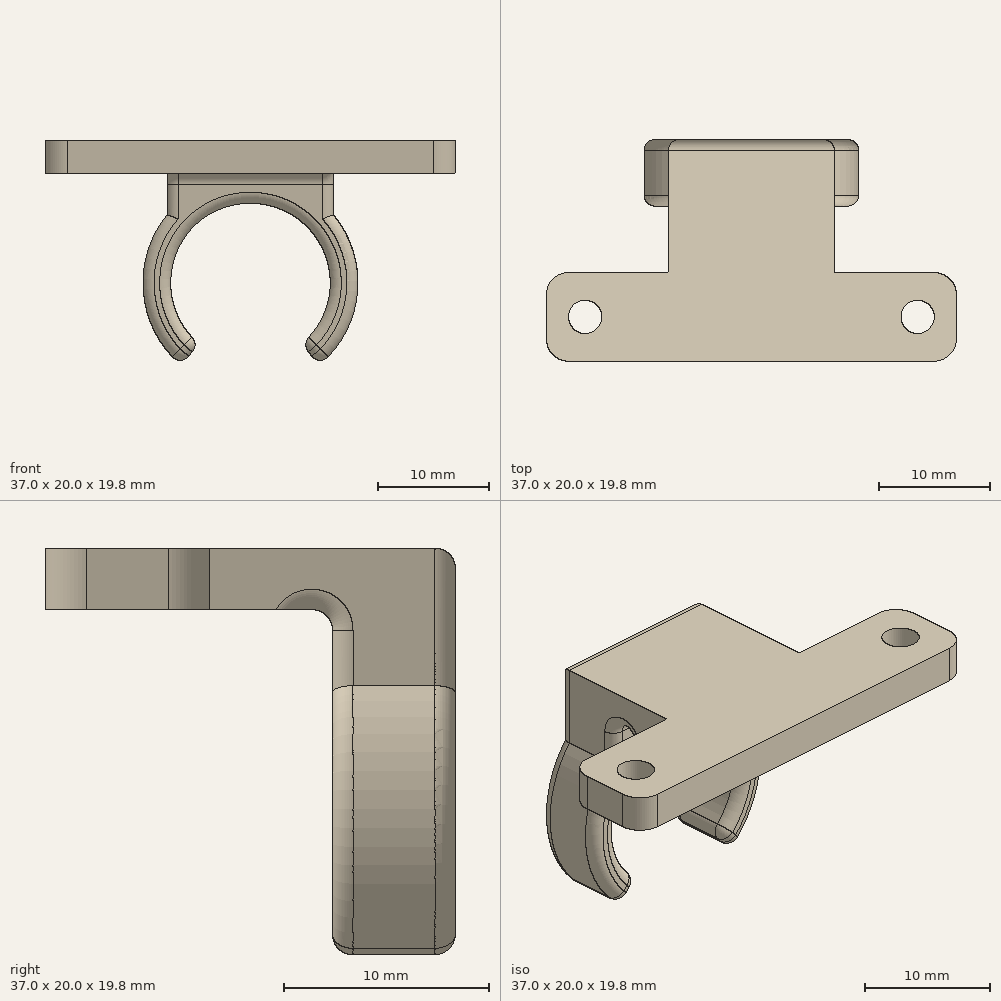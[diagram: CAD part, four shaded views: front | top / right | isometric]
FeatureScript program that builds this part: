
annotation { "Feature Type Name" : "Feature", "Feature Type Description" : "" }
export const myFeature = defineFeature(function(context is Context, id is Id, definition is map)
    precondition{}
    {
        {
            var Q0;
            Q0=qCreatedBy(makeId("Front.planeOp"),FACE);
            var sketch = newSketch(context, id + "F0", { "sketchPlane" : qUnion([Q0])});
            skArc(sketch, "E0", {"start": v(5.27, -4.9) * mm, "mid": v(0, 7.2) * mm, "end": v(-5.27, -4.9) * mm});
            skArc(sketch, "E1.0", {"start": v(7.05, -6.66) * mm, "mid": v(9.7, -0.34) * mm, "end": v(7.5, 6.15) * mm});
            skLineSegment(sketch, "E2", {"start": v(0, 0) * mm, "end": v(6.24, -7.43) * mm, "construction": true});
            skLineSegment(sketch, "E3", {"start": v(5.23, -6.23) * mm, "end": v(5.56, -6.62) * mm});
            skLineSegment(sketch, "E4.MirrorCS", {"start": v(-5.23, -6.23) * mm, "end": v(-5.56, -6.62) * mm});
            skPoint(sketch, "E5.visualSharp", {"position": v(-4.63, -5.52) * mm});
            skArc(sketch, "E5.filletArc", {"start": v(-5.23, -6.23) * mm, "mid": v(-5, -5.57) * mm, "end": v(-5.27, -4.9) * mm});
            skPoint(sketch, "E6.visualSharp", {"position": v(-6.24, -7.43) * mm});
            skArc(sketch, "E6.filletArc", {"start": v(-7.05, -6.66) * mm, "mid": v(-6.3, -6.98) * mm, "end": v(-5.56, -6.62) * mm});
            skPoint(sketch, "E7.visualSharp", {"position": v(4.63, -5.52) * mm});
            skArc(sketch, "E7.filletArc", {"start": v(5.27, -4.9) * mm, "mid": v(5, -5.57) * mm, "end": v(5.23, -6.23) * mm});
            skPoint(sketch, "E8.visualSharp", {"position": v(6.24, -7.43) * mm});
            skArc(sketch, "E8.filletArc", {"start": v(5.56, -6.62) * mm, "mid": v(6.3, -6.98) * mm, "end": v(7.05, -6.66) * mm});
            skLineSegment(sketch, "E9", {"start": v(7.5, 9.86) * mm, "end": v(7.5, 6.15) * mm});
            skArc(sketch, "E10.trimOffspring", {"start": v(-7.5, 6.15) * mm, "mid": v(-9.7, -0.34) * mm, "end": v(-7.05, -6.66) * mm});
            skLineSegment(sketch, "E11", {"start": v(7.5, 9.86) * mm, "end": v(-7.5, 9.86) * mm});
            skLineSegment(sketch, "E12.MirrorCS", {"start": v(-7.5, 9.86) * mm, "end": v(-7.5, 6.15) * mm});
            skSolve(sketch);
        }
        {
            var Q0;
            Q0 = qSketchRegion(id + "F0", true);
            extrude(context, id + "F1", {"entities" : qUnion([Q0]), "depth" : 6 * mm});
        }
        {
            var Q0;
            Q0=makeQuery(id+"F1.opExtrude","CAP_FACE",FACE,{"disambiguationData":[OSD([sQuery(id+"F0.wireOp",EDGE,"E0"),sQuery(id+"F0.wireOp",EDGE,"E1.0"),sQuery(id+"F0.wireOp",EDGE,"E3"),sQuery(id+"F0.wireOp",EDGE,"E4.MirrorCS"),sQuery(id+"F0.wireOp",EDGE,"E5.filletArc"),sQuery(id+"F0.wireOp",EDGE,"E6.filletArc"),sQuery(id+"F0.wireOp",EDGE,"E7.filletArc"),sQuery(id+"F0.wireOp",EDGE,"E8.filletArc"),sQuery(id+"F0.wireOp",EDGE,"UfigFsPe-VwBz-yOrH-qd3c-BaSmVw7mGtwd"),sQuery(id+"F0.wireOp",EDGE,"09a0b145-e03c-4088-8137-e4af93176f2e0.MirrorCS"),sQuery(id+"F0.wireOp",EDGE,"E9"),sQuery(id+"F0.wireOp",EDGE,"LbQmFjFD-MU03-NkMB-9euH-T3eJWOVWMnZS"),sQuery(id+"F0.wireOp",EDGE,"E10.trimOffspring")])],"isStart":true});
            var sketch = newSketch(context, id + "F2", { "sketchPlane" : qUnion([Q0])});
            skLineSegment(sketch, "E13.bottom", {"start": v(-7.5, 9.86) * mm, "end": v(7.5, 9.86) * mm});
            skLineSegment(sketch, "E13.top", {"start": v(-7.5, 12.86) * mm, "end": v(7.5, 12.86) * mm});
            skLineSegment(sketch, "E13.left", {"start": v(-7.5, 9.86) * mm, "end": v(-7.5, 12.86) * mm});
            skLineSegment(sketch, "E13.right", {"start": v(7.5, 9.86) * mm, "end": v(7.5, 12.86) * mm});
            skSolve(sketch);
        }
        {
            var Q0;
            Q0 = qSketchRegion(id + "F2", true);
            extrude(context, id + "F3", {"entities" : qUnion([Q0]), "oppositeDirection" : true, "depth" : 20 * mm});
        }
        {
            var Q0;
            Q0=makeQuery(id+"F3.opExtrude","SWEPT_FACE",FACE,{"disambiguationData":[OSD([sQuery(id+"F2.wireOp",EDGE,"E13.top")])]});
            var sketch = newSketch(context, id + "F4", { "sketchPlane" : qUnion([Q0])});
            skLineSegment(sketch, "E14.bottom", {"start": v(-7.5, -20) * mm, "end": v(-18.5, -20) * mm});
            skLineSegment(sketch, "E14.top", {"start": v(-7.5, -12) * mm, "end": v(-18.5, -12) * mm});
            skLineSegment(sketch, "E14.left", {"start": v(-7.5, -20) * mm, "end": v(-7.5, -12) * mm});
            skLineSegment(sketch, "E14.right", {"start": v(-18.5, -20) * mm, "end": v(-18.5, -12) * mm});
            skLineSegment(sketch, "E15.MirrorCS", {"start": v(7.5, -20) * mm, "end": v(18.5, -20) * mm});
            skLineSegment(sketch, "E16.MirrorCS", {"start": v(7.5, -20) * mm, "end": v(7.5, -12) * mm});
            skLineSegment(sketch, "E17.MirrorCS", {"start": v(7.5, -12) * mm, "end": v(18.5, -12) * mm});
            skLineSegment(sketch, "E18.MirrorCS", {"start": v(18.5, -20) * mm, "end": v(18.5, -12) * mm});
            skLineSegment(sketch, "E19", {"start": v(18.5, -16) * mm, "end": v(-18.5, -16) * mm, "construction": true});
            skCircle(sketch, "E20", {"center": v(-15, -16) * mm, "radius": 1.5 * mm});
            skCircle(sketch, "E21.MirrorC", {"center": v(15, -16) * mm, "radius": 1.5 * mm});
            skSolve(sketch);
        }
        {
            var Q0;
            Q0 = qSketchRegion(id + "F4", true);
            extrude(context, id + "F5", {"entities" : qUnion([Q0]), "oppositeDirection" : true, "depth" : 3 * mm});
        }
        {
            var Q0;
            Q0=makeQuery(id+"F5.opExtrude","SWEPT_BODY",BODY,{"disambiguationData":[OSD([sQuery(id+"F4.wireOp",EDGE,"E14.bottom"),sQuery(id+"F4.wireOp",EDGE,"E14.top"),sQuery(id+"F4.wireOp",EDGE,"E14.left"),sQuery(id+"F4.wireOp",EDGE,"E14.right")])]});
            var Q1;
            Q1=makeQuery(id+"F3.opExtrude","SWEPT_BODY",BODY,{"disambiguationData":[OSD([sQuery(id+"F2.wireOp",EDGE,"E13.bottom"),sQuery(id+"F2.wireOp",EDGE,"E13.top"),sQuery(id+"F2.wireOp",EDGE,"E13.left"),sQuery(id+"F2.wireOp",EDGE,"E13.right")])]});
            var Q2;
            Q2=makeQuery(id+"F5.opExtrude","SWEPT_BODY",BODY,{"disambiguationData":[OSD([sQuery(id+"F4.wireOp",EDGE,"E15.MirrorCS"),sQuery(id+"F4.wireOp",EDGE,"E16.MirrorCS"),sQuery(id+"F4.wireOp",EDGE,"E17.MirrorCS"),sQuery(id+"F4.wireOp",EDGE,"E18.MirrorCS")])]});
            var Q3;
            Q3=makeQuery(id+"F1.opExtrude","SWEPT_BODY",BODY,{"disambiguationData":[OSD([sQuery(id+"F0.wireOp",EDGE,"E0"),sQuery(id+"F0.wireOp",EDGE,"E1.0"),sQuery(id+"F0.wireOp",EDGE,"E3"),sQuery(id+"F0.wireOp",EDGE,"E4.MirrorCS"),sQuery(id+"F0.wireOp",EDGE,"E5.filletArc"),sQuery(id+"F0.wireOp",EDGE,"E6.filletArc"),sQuery(id+"F0.wireOp",EDGE,"E7.filletArc"),sQuery(id+"F0.wireOp",EDGE,"E8.filletArc"),sQuery(id+"F0.wireOp",EDGE,"E9"),sQuery(id+"F0.wireOp",EDGE,"E10.trimOffspring"),sQuery(id+"F0.wireOp",EDGE,"E11"),sQuery(id+"F0.wireOp",EDGE,"E12.MirrorCS")])]});
            booleanBodies(context, id + "F6", {"operationType" : BooleanOperationType.UNION, "tools" : qUnion([Q0, Q1, Q2, Q3])});
        }
        {
            var Q0;
            Q0=makeQuery(id+"F5.opExtrude","SWEPT_EDGE",EDGE,{"disambiguationData":[OSD([sQuery(id+"F4.wireOp",EDGE,"E14.bottom"),sQuery(id+"F4.wireOp",EDGE,"E14.right")])]});
            var Q1;
            Q1=makeQuery(id+"F5.opExtrude","SWEPT_EDGE",EDGE,{"disambiguationData":[OSD([sQuery(id+"F4.wireOp",EDGE,"E14.top"),sQuery(id+"F4.wireOp",EDGE,"E14.right")])]});
            var Q2;
            Q2=makeQuery(id+"F5.opExtrude","SWEPT_EDGE",EDGE,{"disambiguationData":[OSD([sQuery(id+"F4.wireOp",EDGE,"E15.MirrorCS"),sQuery(id+"F4.wireOp",EDGE,"E18.MirrorCS")])]});
            var Q3;
            Q3=makeQuery(id+"F5.opExtrude","SWEPT_EDGE",EDGE,{"disambiguationData":[OSD([sQuery(id+"F4.wireOp",EDGE,"E17.MirrorCS"),sQuery(id+"F4.wireOp",EDGE,"E18.MirrorCS")])]});
            var Q4;
            Q4=makeQuery(id+"F5.opExtrude","SWEPT_EDGE",EDGE,{"disambiguationData":[OSD([sQuery(id+"F2.wireOp",EDGE,"E13.top"),sQuery(id+"F2.wireOp",EDGE,"E13.left"),sQuery(id+"F4.wireOp",EDGE,"E16.MirrorCS"),sQuery(id+"F4.wireOp",EDGE,"E17.MirrorCS")])]});
            var Q5;
            Q5=makeQuery(id+"F5.opExtrude","SWEPT_EDGE",EDGE,{"disambiguationData":[OSD([sQuery(id+"F2.wireOp",EDGE,"E13.top"),sQuery(id+"F2.wireOp",EDGE,"E13.right"),sQuery(id+"F4.wireOp",EDGE,"E14.top"),sQuery(id+"F4.wireOp",EDGE,"E14.left")])]});
            fillet(context, id + "F7", {"entities" : qUnion([Q0, Q1, Q2, Q3, Q4, Q5]), "radius" : 2 * mm, "tangentPropagation" : true, "allowEdgeOverflow" : false});
        }
        {
            var Q0;
            Q0=makeQuery(id+"F6.opBoolean","MERGE",FACE,{"derivedFrom":[makeQuery(id+"F1.opExtrude","CAP_FACE",FACE,{"disambiguationData":[OSD([sQuery(id+"F0.wireOp",EDGE,"E0"),sQuery(id+"F0.wireOp",EDGE,"E1.0"),sQuery(id+"F0.wireOp",EDGE,"E3"),sQuery(id+"F0.wireOp",EDGE,"E4.MirrorCS"),sQuery(id+"F0.wireOp",EDGE,"E5.filletArc"),sQuery(id+"F0.wireOp",EDGE,"E6.filletArc"),sQuery(id+"F0.wireOp",EDGE,"E7.filletArc"),sQuery(id+"F0.wireOp",EDGE,"E8.filletArc"),sQuery(id+"F0.wireOp",EDGE,"E9"),sQuery(id+"F0.wireOp",EDGE,"E10.trimOffspring"),sQuery(id+"F0.wireOp",EDGE,"E11"),sQuery(id+"F0.wireOp",EDGE,"E12.MirrorCS")])],"isStart":true}),makeQuery(id+"F3.opExtrude","CAP_FACE",FACE,{"disambiguationData":[OSD([sQuery(id+"F2.wireOp",EDGE,"E13.bottom"),sQuery(id+"F2.wireOp",EDGE,"E13.top"),sQuery(id+"F2.wireOp",EDGE,"E13.left"),sQuery(id+"F2.wireOp",EDGE,"E13.right")])],"isStart":true})]});
            var Q1;
            Q1=makeQuery(id+"F1.opExtrude","CAP_FACE",FACE,{"disambiguationData":[OSD([sQuery(id+"F0.wireOp",EDGE,"E0"),sQuery(id+"F0.wireOp",EDGE,"E1.0"),sQuery(id+"F0.wireOp",EDGE,"E3"),sQuery(id+"F0.wireOp",EDGE,"E4.MirrorCS"),sQuery(id+"F0.wireOp",EDGE,"E5.filletArc"),sQuery(id+"F0.wireOp",EDGE,"E6.filletArc"),sQuery(id+"F0.wireOp",EDGE,"E7.filletArc"),sQuery(id+"F0.wireOp",EDGE,"E8.filletArc"),sQuery(id+"F0.wireOp",EDGE,"E9"),sQuery(id+"F0.wireOp",EDGE,"E10.trimOffspring"),sQuery(id+"F0.wireOp",EDGE,"E11"),sQuery(id+"F0.wireOp",EDGE,"E12.MirrorCS")])],"isStart":false});
            fillet(context, id + "F8", {"entities" : qUnion([Q0, Q1]), "radius" : 1 * mm, "tangentPropagation" : true, "allowEdgeOverflow" : false});
        }
    });
